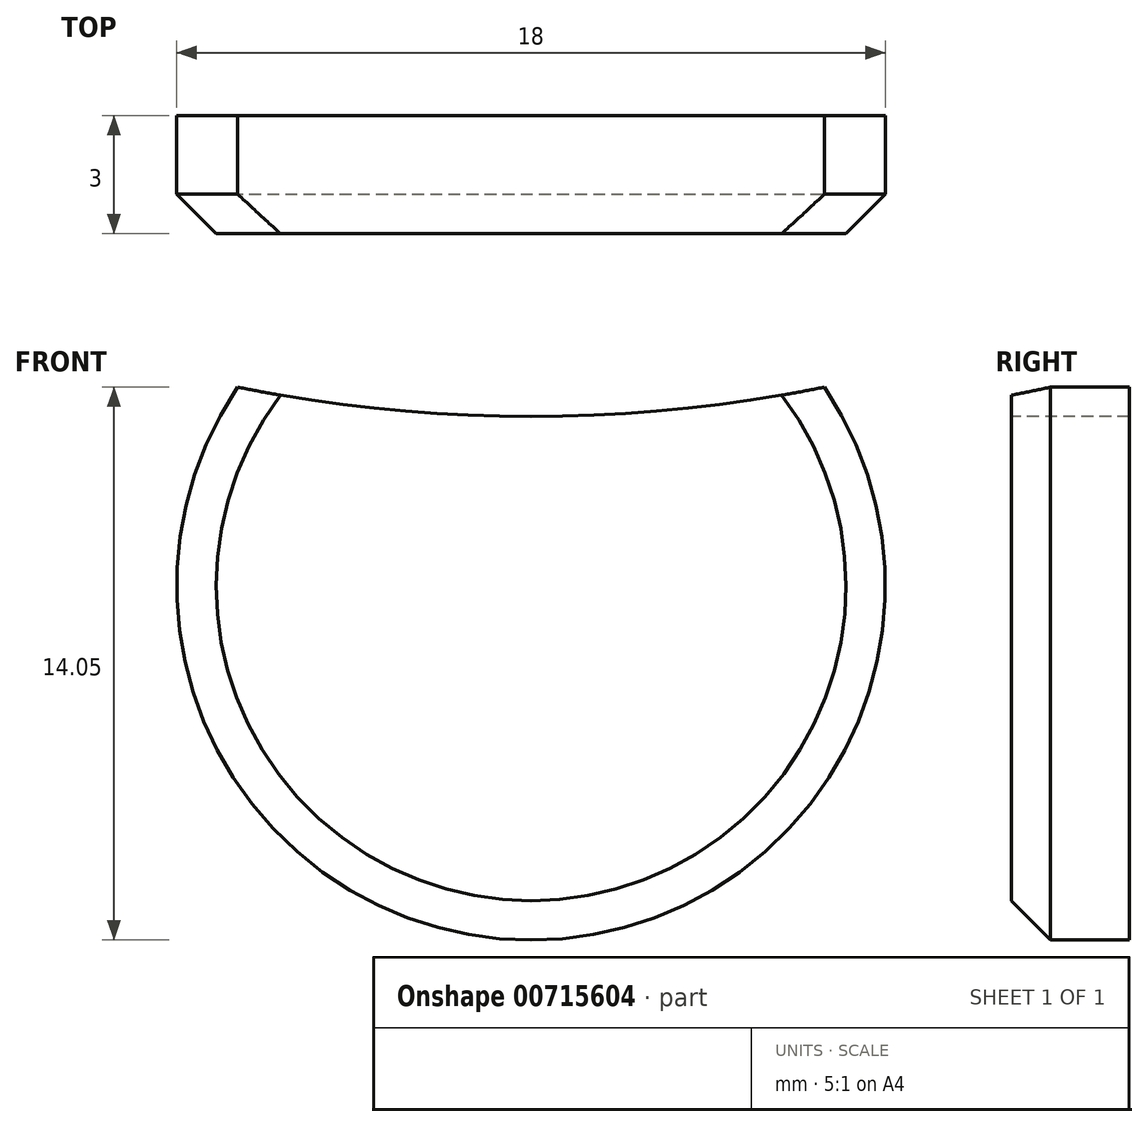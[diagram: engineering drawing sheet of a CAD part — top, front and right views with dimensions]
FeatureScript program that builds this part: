
annotation { "Feature Type Name" : "Feature", "Feature Type Description" : "" }
export const myFeature = defineFeature(function(context is Context, id is Id, definition is map)
    precondition{}
    {
        {
            var Q0;
            Q0=qCreatedBy(makeId("Front.planeOp"),FACE);
            var sketch = newSketch(context, id + "F0", { "sketchPlane" : qUnion([Q0])});
            skCircle(sketch, "E0", {"center": v(0, 0) * mm, "radius": 9 * mm});
            skArc(sketch, "E1", {"start": v(-7.45, 5.05) * mm, "mid": v(0, 4.3) * mm, "end": v(7.45, 5.05) * mm});
            skSolve(sketch);
        }
        {
            var Q0;
            Q0 = qSketchRegion(id + "F0", true);
            extrude(context, id + "F1", {"entities" : qUnion([Q0]), "oppositeDirection" : true, "depth" : 3 * mm, "offsetDistance" : 25 * mm});
        }
        {
            var Q0;
            Q0=makeQuery(id+"F1.opExtrude","CAP_EDGE",EDGE,{"disambiguationData":[OSD([sQuery(id+"F0.wireOp",EDGE,"E0")])],"isStart":true});
            chamfer(context, id + "F2", {"entities" : qUnion([Q0]), "width" : 1 * mm, "tangentPropagation" : true});
        }
        {
            var Q0;
            {var subQ0=sQuery(id+"F0.wireOp",EDGE,"E1");Q0=makeQuery(id+"F0.imprint","IMPRINT",FACE,{"disambiguationData":[TD([[makeQuery(id+"F0.imprint","IMPRINT",EDGE,{"derivedFrom":subQ0}),1.0]])]});}
            extrude(context, id + "F3", {"entities" : qUnion([Q0]), "operationType" : NewBodyOperationType.REMOVE, "endBound" : BoundingType.THROUGH_ALL, "oppositeDirection" : true, "depth" : 25 * mm, "offsetDistance" : 25 * mm});
        }
    });
